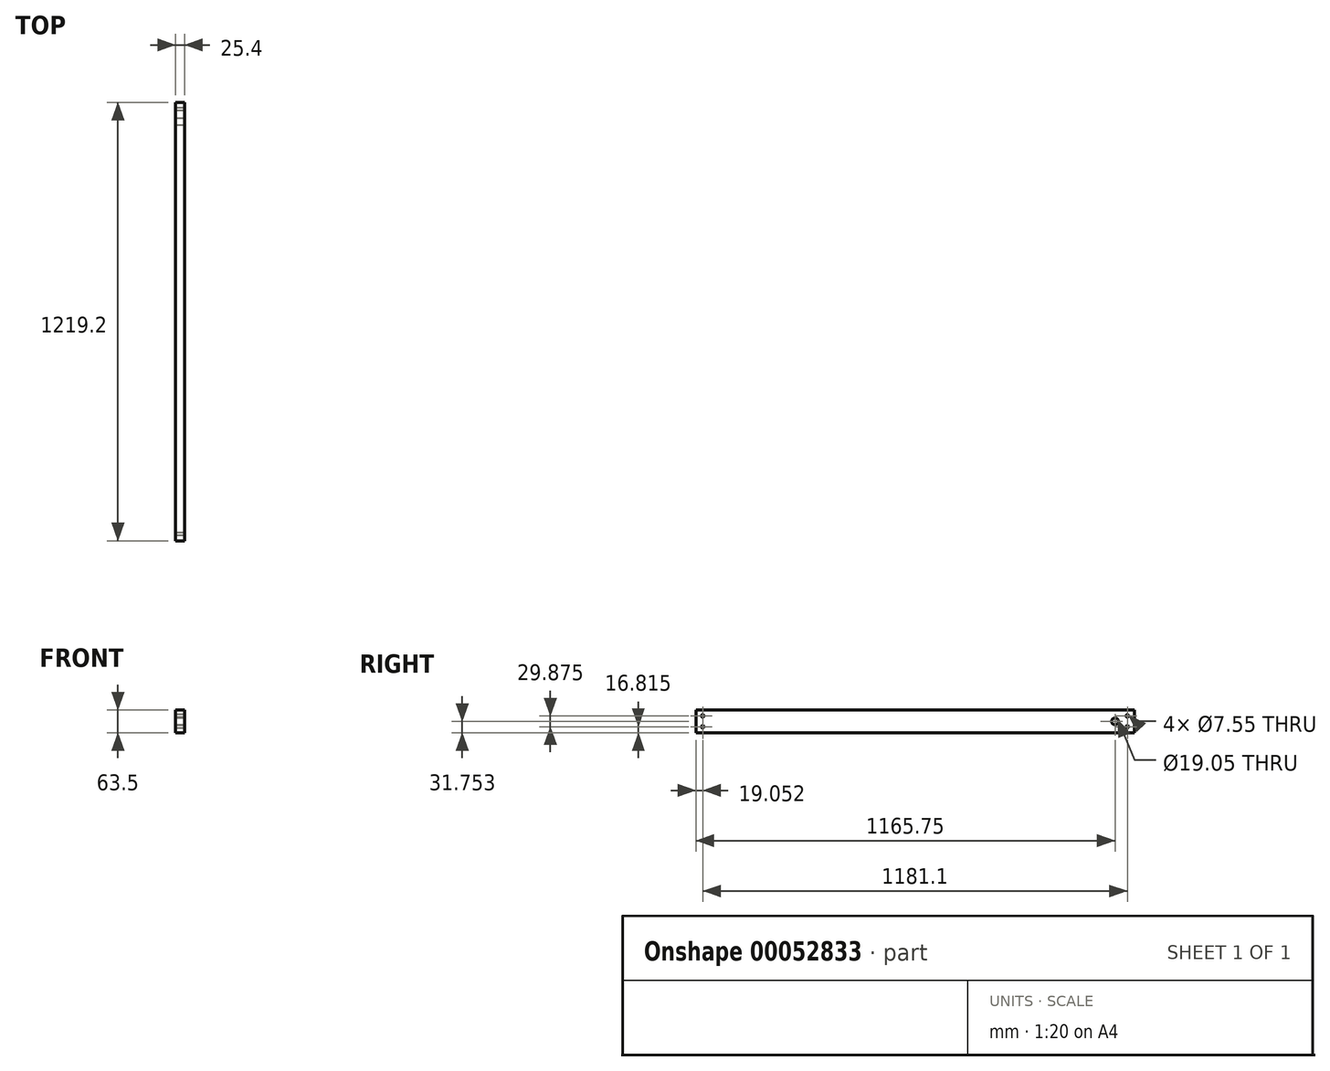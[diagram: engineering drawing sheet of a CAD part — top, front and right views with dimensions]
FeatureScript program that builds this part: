
annotation { "Feature Type Name" : "Feature", "Feature Type Description" : "" }
export const myFeature = defineFeature(function(context is Context, id is Id, definition is map)
    precondition{}
    {
        {
            var Q0;
            Q0=qCreatedBy(makeId("Right.planeOp"),FACE);
            var sketch = newSketch(context, id + "F0", { "sketchPlane" : qUnion([Q0])});
            skLineSegment(sketch, "E0.bottom", {"start": v(-49.89, 68.47) * mm, "end": v(1169.31, 68.47) * mm});
            skLineSegment(sketch, "E0.top", {"start": v(-49.89, 4.97) * mm, "end": v(1169.31, 4.97) * mm});
            skLineSegment(sketch, "E0.left", {"start": v(-49.89, 68.47) * mm, "end": v(-49.89, 4.97) * mm});
            skLineSegment(sketch, "E0.right", {"start": v(1169.31, 68.47) * mm, "end": v(1169.31, 4.97) * mm});
            skLineSegment(sketch, "E1.0", {"start": v(1150.26, 68.47) * mm, "end": v(1150.26, 4.97) * mm});
            skCircle(sketch, "E2", {"center": v(1150.26, 51.66) * mm, "radius": 3.77 * mm});
            skLineSegment(sketch, "E3", {"start": v(1150.26, 36.72) * mm, "end": v(1124.03, 36.72) * mm, "construction": true});
            skCircle(sketch, "E4.MirrorC", {"center": v(1150.26, 21.79) * mm, "radius": 3.77 * mm});
            skLineSegment(sketch, "E5", {"start": v(559.71, 4.97) * mm, "end": v(559.71, 68.47) * mm, "construction": true});
            skCircle(sketch, "E6.MirrorC", {"center": v(-30.84, 51.66) * mm, "radius": 3.77 * mm});
            skCircle(sketch, "E7.MirrorC", {"center": v(-30.84, 21.79) * mm, "radius": 3.77 * mm});
            skSolve(sketch);
        }
        {
            var Q0;
            Q0=qSketchRegion(id+"F0",true);
            extrude(context, id + "F1", {"entities" : qUnion([Q0]), "depth" : 25.4 * mm});
        }
        {
            var Q0;
            Q0=makeQuery(id+"F1.opExtrude","CAP_FACE",FACE,{"disambiguationData":[OSD([sQuery(id+"F0.wireOp",EDGE,"E0.bottom"),sQuery(id+"F0.wireOp",EDGE,"E0.top"),sQuery(id+"F0.wireOp",EDGE,"E0.left"),sQuery(id+"F0.wireOp",EDGE,"E0.right"),sQuery(id+"F0.wireOp",EDGE,"E2"),sQuery(id+"F0.wireOp",EDGE,"E4.MirrorC"),sQuery(id+"F0.wireOp",EDGE,"E6.MirrorC"),sQuery(id+"F0.wireOp",EDGE,"E7.MirrorC")])],"isStart":false});
            var sketch = newSketch(context, id + "F2", { "sketchPlane" : qUnion([Q0])});
            skCircle(sketch, "E8", {"center": v(1115.86, 36.72) * mm, "radius": 9.53 * mm});
            skPoint(sketch, "E8.centerSnap0", {"position": v(1169.31, 36.72) * mm});
            skSolve(sketch);
        }
        {
            var Q0;
            Q0 = qSketchRegion(id + "F2", true);
            extrude(context, id + "F3", {"entities" : qUnion([Q0]), "operationType" : NewBodyOperationType.REMOVE, "endBound" : BoundingType.THROUGH_ALL, "oppositeDirection" : true, "depth" : 25.4 * mm});
        }
    });
